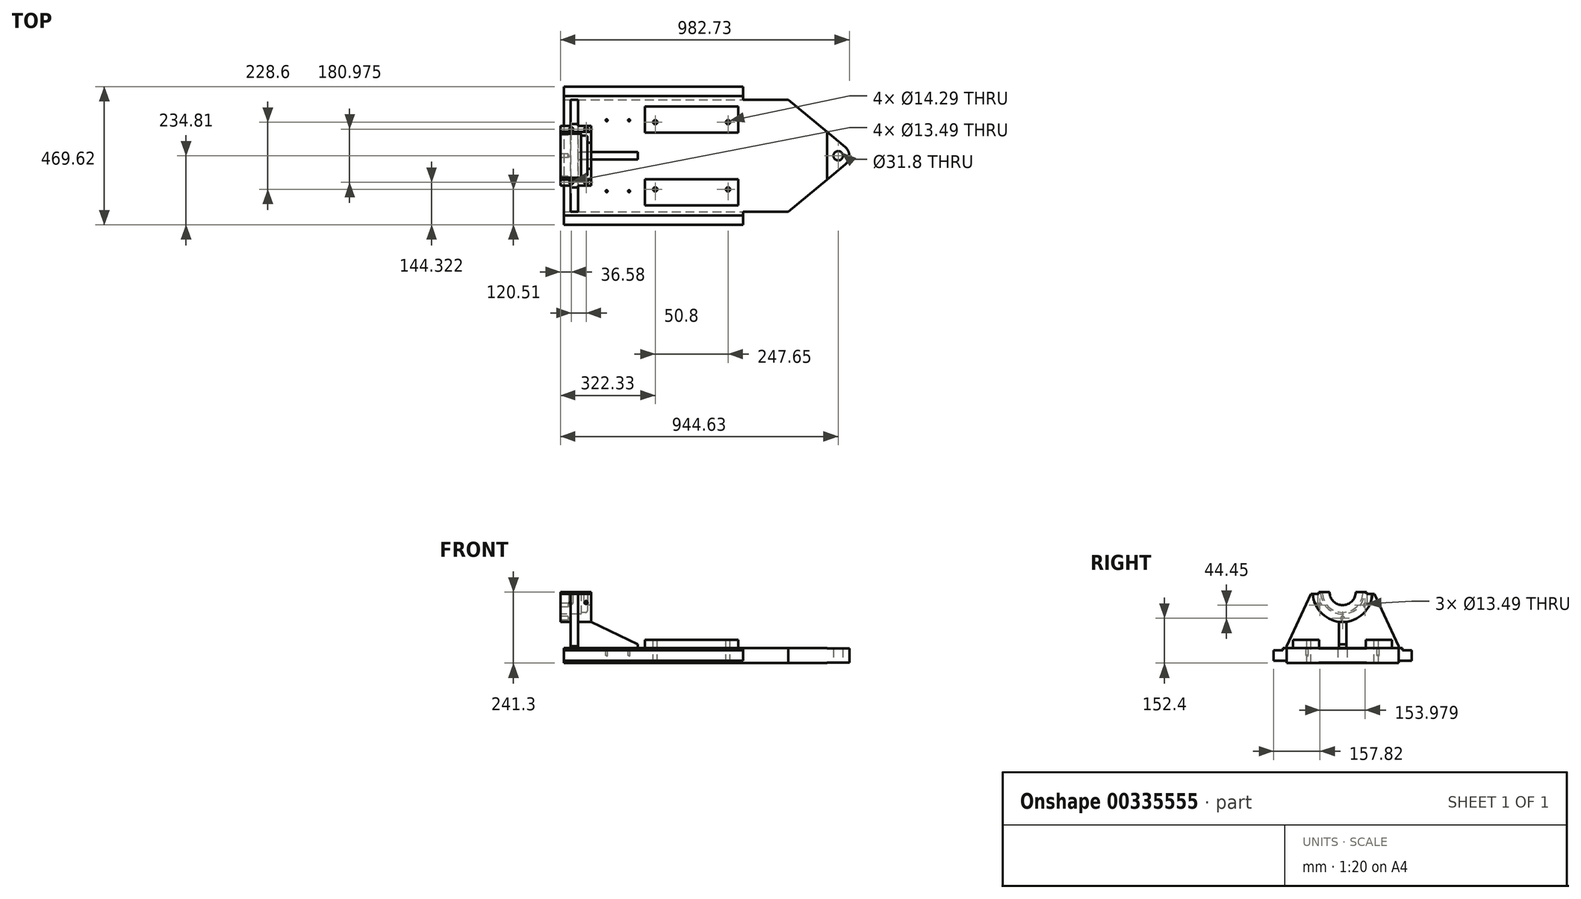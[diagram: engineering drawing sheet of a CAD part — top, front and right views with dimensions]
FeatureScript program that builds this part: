
annotation { "Feature Type Name" : "Feature", "Feature Type Description" : "" }
export const myFeature = defineFeature(function(context is Context, id is Id, definition is map)
    precondition{}
    {
        {
            var Q0;
            Q0=qCreatedBy(makeId("Top.planeOp"),FACE);
            var sketch = newSketch(context, id + "F0", { "sketchPlane" : qUnion([Q0])});
            skLineSegment(sketch, "E0.bottom", {"start": v(-304.8, 234.81) * mm, "end": v(304.8, 234.81) * mm});
            skLineSegment(sketch, "E0.top", {"start": v(-304.8, -234.81) * mm, "end": v(304.8, -234.81) * mm});
            skLineSegment(sketch, "E0.left", {"start": v(-304.8, 234.81) * mm, "end": v(-304.8, -234.81) * mm});
            skPoint(sketch, "E0.middle", {"position": v(0, 0) * mm});
            skLineSegment(sketch, "E1.0", {"start": v(666.75, 234.81) * mm, "end": v(666.75, -234.81) * mm, "construction": true});
            skLineSegment(sketch, "E2.0", {"start": v(628.65, 234.81) * mm, "end": v(628.65, -234.81) * mm, "construction": true});
            skLineSegment(sketch, "E3", {"start": v(459.57, 190.5) * mm, "end": v(653.04, 29.27) * mm});
            skLineSegment(sketch, "E4", {"start": v(459.57, -190.5) * mm, "end": v(656.3, -26.56) * mm});
            skLineSegment(sketch, "E5", {"start": v(304.8, 234.81) * mm, "end": v(304.8, 190.5) * mm});
            skLineSegment(sketch, "E6", {"start": v(-414.48, 0) * mm, "end": v(838.18, 0) * mm, "construction": true});
            skArc(sketch, "E7", {"start": v(653.04, -29.27) * mm, "mid": v(666.75, 0) * mm, "end": v(653.04, 29.27) * mm});
            skCircle(sketch, "E8", {"center": v(628.65, 0) * mm, "radius": 15.9 * mm});
            skLineSegment(sketch, "E9.0", {"start": v(-414.48, -190.5) * mm, "end": v(-304.8, -190.5) * mm});
            skLineSegment(sketch, "E10.trimOffspring", {"start": v(304.8, -190.5) * mm, "end": v(459.57, -190.5) * mm});
            skPoint(sketch, "E11.top.end.orphan", {"position": v(406.4, -234.81) * mm});
            skLineSegment(sketch, "E12.trimOffspring", {"start": v(628.65, -190.5) * mm, "end": v(838.18, -190.5) * mm});
            skLineSegment(sketch, "E13.MirrorCS", {"start": v(304.8, 190.5) * mm, "end": v(459.57, 190.5) * mm});
            skLineSegment(sketch, "E14.trimOffspring", {"start": v(304.8, -190.5) * mm, "end": v(304.8, -234.81) * mm});
            skSolve(sketch);
        }
        {
            var Q0;
            Q0=qSketchRegion(id+"F0",true);
            extrude(context, id + "F1", {"entities" : qUnion([Q0]), "endBound" : BoundingType.SYMMETRIC, "depth" : 50.8 * mm});
        }
        {
            var Q0;
            Q0=makeQuery(id+"F1.opExtrude","CAP_FACE",FACE,{"disambiguationData":[OSD([sQuery(id+"F0.wireOp",EDGE,"E0.bottom"),sQuery(id+"F0.wireOp",EDGE,"E0.top"),sQuery(id+"F0.wireOp",EDGE,"E0.left"),sQuery(id+"F0.wireOp",EDGE,"E3"),sQuery(id+"F0.wireOp",EDGE,"E4"),sQuery(id+"F0.wireOp",EDGE,"E5"),sQuery(id+"F0.wireOp",EDGE,"E7"),sQuery(id+"F0.wireOp",EDGE,"E8"),sQuery(id+"F0.wireOp",EDGE,"E10.trimOffspring"),sQuery(id+"F0.wireOp",EDGE,"E13.MirrorCS"),sQuery(id+"F0.wireOp",EDGE,"E14.trimOffspring")])],"isStart":false});
            var sketch = newSketch(context, id + "F2", { "sketchPlane" : qUnion([Q0])});
            skCircle(sketch, "E15.0", {"center": v(628.65, 0) * mm, "radius": 15.9 * mm, "construction": true});
            skLineSegment(sketch, "E16.bottom", {"start": v(590.55, 101.6) * mm, "end": v(666.75, 101.6) * mm});
            skLineSegment(sketch, "E16.top", {"start": v(590.55, -101.6) * mm, "end": v(666.75, -101.6) * mm});
            skLineSegment(sketch, "E16.left", {"start": v(590.55, 101.6) * mm, "end": v(590.55, -101.6) * mm});
            skLineSegment(sketch, "E16.right", {"start": v(666.75, 101.6) * mm, "end": v(666.75, -101.6) * mm});
            skSolve(sketch);
        }
        {
            var Q0;
            Q0=qSketchRegion(id+"F2",true);
            extrude(context, id + "F3", {"entities" : qUnion([Q0]), "operationType" : NewBodyOperationType.REMOVE, "oppositeDirection" : true, "depth" : 1.59 * mm});
        }
        {
            var Q0;
            Q0=makeQuery(id+"F1.opExtrude","CAP_FACE",FACE,{"disambiguationData":[OSD([sQuery(id+"F0.wireOp",EDGE,"E0.bottom"),sQuery(id+"F0.wireOp",EDGE,"E0.top"),sQuery(id+"F0.wireOp",EDGE,"E0.left"),sQuery(id+"F0.wireOp",EDGE,"E3"),sQuery(id+"F0.wireOp",EDGE,"E4"),sQuery(id+"F0.wireOp",EDGE,"E5"),sQuery(id+"F0.wireOp",EDGE,"E7"),sQuery(id+"F0.wireOp",EDGE,"E8"),sQuery(id+"F0.wireOp",EDGE,"E10.trimOffspring"),sQuery(id+"F0.wireOp",EDGE,"E13.MirrorCS"),sQuery(id+"F0.wireOp",EDGE,"E14.trimOffspring")])],"isStart":true});
            var sketch = newSketch(context, id + "F4", { "sketchPlane" : qUnion([Q0])});
            skCircle(sketch, "E17.0", {"center": v(628.65, 0) * mm, "radius": 15.9 * mm, "construction": true});
            skLineSegment(sketch, "E18.bottom", {"start": v(590.55, 101.6) * mm, "end": v(666.75, 101.6) * mm});
            skLineSegment(sketch, "E18.top", {"start": v(590.55, -101.6) * mm, "end": v(666.75, -101.6) * mm});
            skLineSegment(sketch, "E18.left", {"start": v(590.55, 101.6) * mm, "end": v(590.55, -101.6) * mm});
            skLineSegment(sketch, "E18.right", {"start": v(666.75, 101.6) * mm, "end": v(666.75, -101.6) * mm});
            skSolve(sketch);
        }
        {
            var Q0;
            Q0=qSketchRegion(id+"F4",true);
            extrude(context, id + "F5", {"entities" : qUnion([Q0]), "operationType" : NewBodyOperationType.REMOVE, "oppositeDirection" : true, "depth" : 1.59 * mm});
        }
        {
            var Q0;
            Q0=makeQuery(id+"F1.opExtrude","CAP_FACE",FACE,{"disambiguationData":[OSD([sQuery(id+"F0.wireOp",EDGE,"E0.bottom"),sQuery(id+"F0.wireOp",EDGE,"E0.top"),sQuery(id+"F0.wireOp",EDGE,"E0.left"),sQuery(id+"F0.wireOp",EDGE,"E3"),sQuery(id+"F0.wireOp",EDGE,"E4"),sQuery(id+"F0.wireOp",EDGE,"E5"),sQuery(id+"F0.wireOp",EDGE,"E7"),sQuery(id+"F0.wireOp",EDGE,"E8"),sQuery(id+"F0.wireOp",EDGE,"E10.trimOffspring"),sQuery(id+"F0.wireOp",EDGE,"E13.MirrorCS"),sQuery(id+"F0.wireOp",EDGE,"E14.trimOffspring")])],"isStart":false});
            var sketch = newSketch(context, id + "F6", { "sketchPlane" : qUnion([Q0])});
            skLineSegment(sketch, "E19", {"start": v(-362.8, 0) * mm, "end": v(684.09, 0) * mm, "construction": true});
            skLineSegment(sketch, "E20.0", {"start": v(-362.8, -203.2) * mm, "end": v(684.09, -203.2) * mm, "construction": true});
            skLineSegment(sketch, "E21.0", {"start": v(-304.8, 234.81) * mm, "end": v(-304.8, -234.81) * mm, "construction": true});
            skLineSegment(sketch, "E22.0", {"start": v(304.8, -190.5) * mm, "end": v(304.8, -234.81) * mm, "construction": true});
            skLineSegment(sketch, "E23.bottom", {"start": v(-304.8, -234.81) * mm, "end": v(332.24, -234.81) * mm});
            skLineSegment(sketch, "E23.top", {"start": v(-304.8, -203.2) * mm, "end": v(332.24, -203.2) * mm});
            skLineSegment(sketch, "E23.left", {"start": v(-304.8, -234.81) * mm, "end": v(-304.8, -203.2) * mm});
            skLineSegment(sketch, "E23.right", {"start": v(332.24, -234.81) * mm, "end": v(332.24, -203.2) * mm});
            skLineSegment(sketch, "E24.MirrorCS", {"start": v(332.24, 234.81) * mm, "end": v(332.24, 203.2) * mm});
            skLineSegment(sketch, "E25.MirrorCS", {"start": v(-304.8, 234.81) * mm, "end": v(-304.8, 203.2) * mm});
            skLineSegment(sketch, "E26.MirrorCS", {"start": v(-304.8, 203.2) * mm, "end": v(332.24, 203.2) * mm});
            skLineSegment(sketch, "E27.MirrorCS", {"start": v(-304.8, 234.81) * mm, "end": v(332.24, 234.81) * mm});
            skLineSegment(sketch, "E28.MirrorCS", {"start": v(304.8, 190.5) * mm, "end": v(304.8, 234.81) * mm, "construction": true});
            skSolve(sketch);
        }
        {
            var Q0;
            Q0=qSketchRegion(id+"F6",true);
            extrude(context, id + "F7", {"entities" : qUnion([Q0]), "operationType" : NewBodyOperationType.REMOVE, "oppositeDirection" : true, "depth" : 7.94 * mm});
        }
        {
            var Q0;
            Q0=makeQuery(id+"F1.opExtrude","CAP_FACE",FACE,{"disambiguationData":[OSD([sQuery(id+"F0.wireOp",EDGE,"E0.bottom"),sQuery(id+"F0.wireOp",EDGE,"E0.top"),sQuery(id+"F0.wireOp",EDGE,"E0.left"),sQuery(id+"F0.wireOp",EDGE,"E3"),sQuery(id+"F0.wireOp",EDGE,"E4"),sQuery(id+"F0.wireOp",EDGE,"E5"),sQuery(id+"F0.wireOp",EDGE,"E7"),sQuery(id+"F0.wireOp",EDGE,"E8"),sQuery(id+"F0.wireOp",EDGE,"E10.trimOffspring"),sQuery(id+"F0.wireOp",EDGE,"E13.MirrorCS"),sQuery(id+"F0.wireOp",EDGE,"E14.trimOffspring")])],"isStart":true});
            var sketch = newSketch(context, id + "F8", { "sketchPlane" : qUnion([Q0])});
            skLineSegment(sketch, "E29", {"start": v(-400.34, 0) * mm, "end": v(753.76, 0) * mm, "construction": true});
            skLineSegment(sketch, "E30.0", {"start": v(-304.8, -234.81) * mm, "end": v(-304.8, 234.81) * mm, "construction": true});
            skLineSegment(sketch, "E31.0", {"start": v(-400.34, -190.5) * mm, "end": v(753.76, -190.5) * mm, "construction": true});
            skLineSegment(sketch, "E32.bottom", {"start": v(-304.8, -190.5) * mm, "end": v(475.01, -190.5) * mm});
            skLineSegment(sketch, "E32.top", {"start": v(-304.8, -283.73) * mm, "end": v(475.01, -283.73) * mm});
            skLineSegment(sketch, "E32.left", {"start": v(-304.8, -190.5) * mm, "end": v(-304.8, -283.73) * mm});
            skLineSegment(sketch, "E32.right", {"start": v(475.01, -190.5) * mm, "end": v(475.01, -283.73) * mm});
            skLineSegment(sketch, "E33.MirrorCS", {"start": v(475.01, 190.5) * mm, "end": v(475.01, 283.73) * mm});
            skLineSegment(sketch, "E34.MirrorCS", {"start": v(-304.8, 190.5) * mm, "end": v(-304.8, 283.73) * mm});
            skLineSegment(sketch, "E35.MirrorCS", {"start": v(-304.8, 283.73) * mm, "end": v(475.01, 283.73) * mm});
            skLineSegment(sketch, "E36.MirrorCS", {"start": v(-304.8, 190.5) * mm, "end": v(475.01, 190.5) * mm});
            skSolve(sketch);
        }
        {
            var Q0;
            Q0=qSketchRegion(id+"F8",true);
            extrude(context, id + "F9", {"entities" : qUnion([Q0]), "operationType" : NewBodyOperationType.REMOVE, "oppositeDirection" : true, "depth" : 7.94 * mm});
        }
        {
            var Q0;
            Q0=makeQuery(id+"F1.opExtrude","CAP_FACE",FACE,{"disambiguationData":[OSD([sQuery(id+"F0.wireOp",EDGE,"E0.bottom"),sQuery(id+"F0.wireOp",EDGE,"E0.top"),sQuery(id+"F0.wireOp",EDGE,"E0.left"),sQuery(id+"F0.wireOp",EDGE,"E3"),sQuery(id+"F0.wireOp",EDGE,"E4"),sQuery(id+"F0.wireOp",EDGE,"E5"),sQuery(id+"F0.wireOp",EDGE,"E7"),sQuery(id+"F0.wireOp",EDGE,"E8"),sQuery(id+"F0.wireOp",EDGE,"E10.trimOffspring"),sQuery(id+"F0.wireOp",EDGE,"E13.MirrorCS"),sQuery(id+"F0.wireOp",EDGE,"E14.trimOffspring")])],"isStart":false});
            var sketch = newSketch(context, id + "F10", { "sketchPlane" : qUnion([Q0])});
            skLineSegment(sketch, "E37", {"start": v(-417.52, 0) * mm, "end": v(724.3, 0) * mm, "construction": true});
            skLineSegment(sketch, "E38.0", {"start": v(-304.8, 203.2) * mm, "end": v(-304.8, -203.2) * mm, "construction": true});
            skLineSegment(sketch, "E39.0", {"start": v(-28.57, 203.2) * mm, "end": v(-28.57, -203.2) * mm, "construction": true});
            skLineSegment(sketch, "E40.0", {"start": v(288.93, 203.2) * mm, "end": v(288.93, -203.2) * mm, "construction": true});
            skLineSegment(sketch, "E41.0", {"start": v(-417.52, -79.38) * mm, "end": v(724.3, -79.38) * mm, "construction": true});
            skLineSegment(sketch, "E42.bottom", {"start": v(-28.57, -79.38) * mm, "end": v(288.93, -79.38) * mm});
            skLineSegment(sketch, "E42.top", {"start": v(-28.57, -168.28) * mm, "end": v(288.93, -168.28) * mm});
            skLineSegment(sketch, "E42.left", {"start": v(-28.57, -79.38) * mm, "end": v(-28.57, -168.28) * mm});
            skLineSegment(sketch, "E42.right", {"start": v(288.93, -79.38) * mm, "end": v(288.93, -168.28) * mm});
            skLineSegment(sketch, "E43.MirrorCS", {"start": v(-28.57, 168.28) * mm, "end": v(288.93, 168.28) * mm});
            skLineSegment(sketch, "E44.MirrorCS", {"start": v(288.93, 79.38) * mm, "end": v(288.93, 168.28) * mm});
            skLineSegment(sketch, "E45.MirrorCS", {"start": v(-28.57, 79.38) * mm, "end": v(-28.57, 168.28) * mm});
            skLineSegment(sketch, "E46.MirrorCS", {"start": v(-28.57, 79.38) * mm, "end": v(288.93, 79.38) * mm});
            skSolve(sketch);
        }
        {
            var Q0;
            Q0=qSketchRegion(id+"F10",true);
            extrude(context, id + "F11", {"entities" : qUnion([Q0]), "operationType" : NewBodyOperationType.ADD, "depth" : 28.57 * mm});
        }
        {
            var Q0;
            Q0=makeQuery(id+"F11.opExtrude","CAP_FACE",FACE,{"disambiguationData":[OSD([sQuery(id+"F10.wireOp",EDGE,"E43.MirrorCS"),sQuery(id+"F10.wireOp",EDGE,"E44.MirrorCS"),sQuery(id+"F10.wireOp",EDGE,"E45.MirrorCS"),sQuery(id+"F10.wireOp",EDGE,"E46.MirrorCS")])],"isStart":false});
            var sketch = newSketch(context, id + "F12", { "sketchPlane" : qUnion([Q0])});
            skCircle(sketch, "E47.0", {"center": v(628.65, 0) * mm, "radius": 15.9 * mm, "construction": true});
            skLineSegment(sketch, "E48", {"start": v(628.65, 0) * mm, "end": v(628.65, 304) * mm, "construction": true});
            skLineSegment(sketch, "E49", {"start": v(-454.06, 0) * mm, "end": v(702.68, 0) * mm, "construction": true});
            skLineSegment(sketch, "E50.0", {"start": v(-454.06, 114.3) * mm, "end": v(702.68, 114.3) * mm, "construction": true});
            skLineSegment(sketch, "E51.0", {"start": v(254, 0) * mm, "end": v(254, 304) * mm, "construction": true});
            skLineSegment(sketch, "E52.0", {"start": v(6.35, 0) * mm, "end": v(6.35, 304) * mm, "construction": true});
            skPoint(sketch, "E53", {"position": v(6.35, 114.3) * mm});
            skPoint(sketch, "E54", {"position": v(254, 114.3) * mm});
            skPoint(sketch, "E55.MirrorP", {"position": v(254, -114.3) * mm});
            skPoint(sketch, "E56.MirrorP", {"position": v(6.35, -114.3) * mm});
            skSolve(sketch);
        }
        {
            var Q0;
            Q0=sQuery(id+"F12.wireOp",VERTEX,"E53");
            var Q1;
            Q1=sQuery(id+"F12.wireOp",VERTEX,"E54");
            var Q2;
            Q2=sQuery(id+"F12.wireOp",VERTEX,"E56.MirrorP");
            var Q3;
            Q3=sQuery(id+"F12.wireOp",VERTEX,"E55.MirrorP");
            var Q4;
            Q4=makeQuery(id+"F1.opExtrude","SWEPT_BODY",BODY,{"disambiguationData":[OSD([sQuery(id+"F0.wireOp",EDGE,"E0.bottom"),sQuery(id+"F0.wireOp",EDGE,"E0.top"),sQuery(id+"F0.wireOp",EDGE,"E0.left"),sQuery(id+"F0.wireOp",EDGE,"E3"),sQuery(id+"F0.wireOp",EDGE,"E4"),sQuery(id+"F0.wireOp",EDGE,"E5"),sQuery(id+"F0.wireOp",EDGE,"E7"),sQuery(id+"F0.wireOp",EDGE,"E8"),sQuery(id+"F0.wireOp",EDGE,"E10.trimOffspring"),sQuery(id+"F0.wireOp",EDGE,"E13.MirrorCS"),sQuery(id+"F0.wireOp",EDGE,"E14.trimOffspring")])]});
            hole(context, id + "F13", {"style" : HoleStyle.SIMPLE, "endStyle" : HoleEndStyle.THROUGH, "holeDiameter" : 14.29 * mm, "tappedDepth" : 19.53 * mm, "tapClearance" : 3, "locations" : qUnion([Q0, Q1, Q2, Q3]), "scope" : qUnion([Q4])});
        }
        {
            var Q0;
            Q0=makeQuery(id+"F1.opExtrude","CAP_FACE",FACE,{"disambiguationData":[OSD([sQuery(id+"F0.wireOp",EDGE,"E0.bottom"),sQuery(id+"F0.wireOp",EDGE,"E0.top"),sQuery(id+"F0.wireOp",EDGE,"E0.left"),sQuery(id+"F0.wireOp",EDGE,"E3"),sQuery(id+"F0.wireOp",EDGE,"E4"),sQuery(id+"F0.wireOp",EDGE,"E5"),sQuery(id+"F0.wireOp",EDGE,"E7"),sQuery(id+"F0.wireOp",EDGE,"E8"),sQuery(id+"F0.wireOp",EDGE,"E10.trimOffspring"),sQuery(id+"F0.wireOp",EDGE,"E13.MirrorCS"),sQuery(id+"F0.wireOp",EDGE,"E14.trimOffspring")])],"isStart":false});
            var sketch = newSketch(context, id + "F14", { "sketchPlane" : qUnion([Q0])});
            skLineSegment(sketch, "E57.0", {"start": v(-304.8, 203.2) * mm, "end": v(-304.8, -203.2) * mm, "construction": true});
            skLineSegment(sketch, "E58.0", {"start": v(-280.99, 203.2) * mm, "end": v(-280.99, -203.2) * mm, "construction": true});
            skLineSegment(sketch, "E59", {"start": v(-408.3, 0) * mm, "end": v(198.31, 0) * mm, "construction": true});
            skLineSegment(sketch, "E60.0", {"start": v(-408.3, -190.5) * mm, "end": v(198.31, -190.5) * mm, "construction": true});
            skLineSegment(sketch, "E61.bottom", {"start": v(-280.99, -190.5) * mm, "end": v(-255.59, -190.5) * mm});
            skLineSegment(sketch, "E61.top", {"start": v(-280.99, 190.5) * mm, "end": v(-255.59, 190.5) * mm});
            skLineSegment(sketch, "E61.left", {"start": v(-280.99, -190.5) * mm, "end": v(-280.99, 190.5) * mm});
            skLineSegment(sketch, "E61.right", {"start": v(-255.59, -190.5) * mm, "end": v(-255.59, 190.5) * mm});
            skSolve(sketch);
        }
        {
            var Q0;
            Q0=qSketchRegion(id+"F14",true);
            extrude(context, id + "F15", {"entities" : qUnion([Q0]), "operationType" : NewBodyOperationType.ADD, "depth" : 190.5 * mm});
        }
        {
            var Q0;
            Q0=makeQuery(id+"F1.opExtrude","SWEPT_FACE",FACE,{"disambiguationData":[OSD([sQuery(id+"F0.wireOp",EDGE,"E0.left")])]});
            cPlane(context, id + "F16", {"entities" : qUnion([Q0]), "cplaneType" : CPlaneType.OFFSET, "offset" : 11.18 * mm, "width" : 152.4 * mm, "height" : 152.4 * mm});
        }
        {
            var Q0;
            Q0=qCreatedBy(id+"F16.planeOp",FACE);
            var sketch = newSketch(context, id + "F17", { "sketchPlane" : qUnion([Q0])});
            skLineSegment(sketch, "E62.0", {"start": v(190.5, 215.9) * mm, "end": v(-190.5, 215.9) * mm, "construction": true});
            skLineSegment(sketch, "E63", {"start": v(0, 334.76) * mm, "end": v(0, -159.92) * mm, "construction": true});
            skCircle(sketch, "E64", {"center": v(0, 215.9) * mm, "radius": 101.6 * mm});
            skSolve(sketch);
        }
        {
            var Q0;
            Q0=qSketchRegion(id+"F17",true);
            extrude(context, id + "F18", {"entities" : qUnion([Q0]), "operationType" : NewBodyOperationType.ADD, "oppositeDirection" : true, "depth" : 104.77 * mm});
        }
        {
            var Q0;
            Q0=makeQuery(id+"F15.opExtrude","SWEPT_FACE",FACE,{"disambiguationData":[OSD([sQuery(id+"F14.wireOp",EDGE,"E61.left")])]});
            var sketch = newSketch(context, id + "F19", { "sketchPlane" : qUnion([Q0])});
            skCircle(sketch, "E65.0", {"center": v(0, 215.9) * mm, "radius": 101.6 * mm, "construction": true});
            skLineSegment(sketch, "E66.0", {"start": v(-203.2, 31.75) * mm, "end": v(203.2, 31.75) * mm, "construction": true});
            skLineSegment(sketch, "E67.0", {"start": v(-190.5, 215.9) * mm, "end": v(-190.5, 25.4) * mm, "construction": true});
            skLineSegment(sketch, "E68", {"start": v(-190.5, 31.75) * mm, "end": v(-107.95, 209.55) * mm});
            skLineSegment(sketch, "E69", {"start": v(-107.95, 209.55) * mm, "end": v(-80.96, 209.55) * mm});
            skLineSegment(sketch, "E70", {"start": v(-80.96, 209.55) * mm, "end": v(-80.96, 215.9) * mm});
            skLineSegment(sketch, "E71", {"start": v(-80.96, 215.9) * mm, "end": v(0, 215.9) * mm});
            skLineSegment(sketch, "E72", {"start": v(0, 356.38) * mm, "end": v(0, -105.82) * mm, "construction": true});
            skLineSegment(sketch, "E73.MirrorCS", {"start": v(80.96, 209.55) * mm, "end": v(80.96, 215.9) * mm});
            skLineSegment(sketch, "E74.MirrorCS", {"start": v(80.96, 215.9) * mm, "end": v(0, 215.9) * mm});
            skLineSegment(sketch, "E75.MirrorCS", {"start": v(190.5, 31.75) * mm, "end": v(107.95, 209.55) * mm});
            skLineSegment(sketch, "E76.MirrorCS", {"start": v(190.5, 215.9) * mm, "end": v(190.5, 25.4) * mm, "construction": true});
            skLineSegment(sketch, "E77.MirrorCS", {"start": v(107.95, 209.55) * mm, "end": v(80.96, 209.55) * mm});
            skLineSegment(sketch, "E78", {"start": v(-190.5, 31.75) * mm, "end": v(-190.5, 348.54) * mm});
            skLineSegment(sketch, "E79", {"start": v(-190.5, 348.54) * mm, "end": v(190.5, 348.54) * mm});
            skLineSegment(sketch, "E80", {"start": v(190.5, 348.54) * mm, "end": v(190.5, 31.75) * mm});
            skSolve(sketch);
        }
        {
            var Q0;
            Q0=qSketchRegion(id+"F19",true);
            extrude(context, id + "F20", {"entities" : qUnion([Q0]), "operationType" : NewBodyOperationType.REMOVE, "endBound" : BoundingType.SYMMETRIC, "oppositeDirection" : true, "depth" : 152.4 * mm});
        }
        {
            var Q0;
            Q0=makeQuery(id+"F18.opExtrude","CAP_FACE",FACE,{"disambiguationData":[OSD([sQuery(id+"F17.wireOp",EDGE,"E64")])],"isStart":true});
            var sketch = newSketch(context, id + "F21", { "sketchPlane" : qUnion([Q0])});
            skCircle(sketch, "E81", {"center": v(0, 215.9) * mm, "radius": 44.45 * mm});
            skSolve(sketch);
        }
        {
            var Q0;
            Q0=qSketchRegion(id+"F21",true);
            extrude(context, id + "F22", {"entities" : qUnion([Q0]), "operationType" : NewBodyOperationType.REMOVE, "endBound" : BoundingType.THROUGH_ALL, "oppositeDirection" : true, "depth" : 25.4 * mm});
        }
        {
            var Q0;
            Q0=makeQuery(id+"F18.opExtrude","CAP_FACE",FACE,{"disambiguationData":[OSD([sQuery(id+"F17.wireOp",EDGE,"E64")])],"isStart":true});
            var sketch = newSketch(context, id + "F23", { "sketchPlane" : qUnion([Q0])});
            skArc(sketch, "E82.0", {"start": v(-44.45, 215.9) * mm, "mid": v(0, 171.45) * mm, "end": v(44.45, 215.9) * mm, "construction": true});
            skCircle(sketch, "E83", {"center": v(0, 215.9) * mm, "radius": 69.09 * mm});
            skSolve(sketch);
        }
        {
            var Q0;
            Q0=qSketchRegion(id+"F23",true);
            extrude(context, id + "F24", {"entities" : qUnion([Q0]), "operationType" : NewBodyOperationType.REMOVE, "oppositeDirection" : true, "depth" : 92.07 * mm});
        }
        {
            var Q0;
            Q0=makeQuery(id+"F18.opExtrude","CAP_FACE",FACE,{"disambiguationData":[OSD([sQuery(id+"F17.wireOp",EDGE,"E64")])],"isStart":true});
            var sketch = newSketch(context, id + "F25", { "sketchPlane" : qUnion([Q0])});
            skArc(sketch, "E84.0", {"start": v(44.45, 215.9) * mm, "mid": v(0, 171.45) * mm, "end": v(-44.45, 215.9) * mm, "construction": true});
            skCircle(sketch, "E85", {"center": v(0, 215.9) * mm, "radius": 74.93 * mm});
            skSolve(sketch);
        }
        {
            var Q0;
            Q0=qSketchRegion(id+"F25",true);
            extrude(context, id + "F26", {"entities" : qUnion([Q0]), "operationType" : NewBodyOperationType.REMOVE, "oppositeDirection" : true, "depth" : 69.85 * mm});
        }
        {
            var Q0;
            Q0=makeQuery(id+"F20.boolean.opBoolean","COPY",FACE,{"derivedFrom":makeQuery(id+"F20.opExtrude","SWEPT_FACE",FACE,{"disambiguationData":[OSD([sQuery(id+"F19.wireOp",EDGE,"E69")])]})});
            var sketch = newSketch(context, id + "F27", { "sketchPlane" : qUnion([Q0])});
            skLineSegment(sketch, "E86", {"start": v(-429.52, 0) * mm, "end": v(-135.24, 0) * mm, "construction": true});
            skLineSegment(sketch, "E87.0", {"start": v(-315.98, 101.4) * mm, "end": v(-315.98, 80.96) * mm, "construction": true});
            skLineSegment(sketch, "E88.0", {"start": v(-429.52, 90.49) * mm, "end": v(-135.24, 90.49) * mm, "construction": true});
            skLineSegment(sketch, "E89.0", {"start": v(-279.4, 101.4) * mm, "end": v(-279.4, 80.96) * mm, "construction": true});
            skLineSegment(sketch, "E90.0", {"start": v(-228.6, 101.4) * mm, "end": v(-228.6, 80.96) * mm, "construction": true});
            skPoint(sketch, "E91", {"position": v(-279.4, 90.49) * mm});
            skPoint(sketch, "E92", {"position": v(-228.6, 90.49) * mm});
            skPoint(sketch, "E93.MirrorP", {"position": v(-279.4, -90.49) * mm});
            skPoint(sketch, "E94.MirrorP", {"position": v(-228.6, -90.49) * mm});
            skSolve(sketch);
        }
        {
            var Q0;
            Q0=sQuery(id+"F27.wireOp",VERTEX,"E91");
            var Q1;
            Q1=sQuery(id+"F27.wireOp",VERTEX,"E92");
            var Q2;
            Q2=sQuery(id+"F27.wireOp",VERTEX,"E93.MirrorP");
            var Q3;
            Q3=sQuery(id+"F27.wireOp",VERTEX,"E94.MirrorP");
            var Q4;
            Q4=makeQuery(id+"F1.opExtrude","SWEPT_BODY",BODY,{"disambiguationData":[OSD([sQuery(id+"F0.wireOp",EDGE,"E0.bottom"),sQuery(id+"F0.wireOp",EDGE,"E0.top"),sQuery(id+"F0.wireOp",EDGE,"E0.left"),sQuery(id+"F0.wireOp",EDGE,"E3"),sQuery(id+"F0.wireOp",EDGE,"E4"),sQuery(id+"F0.wireOp",EDGE,"E5"),sQuery(id+"F0.wireOp",EDGE,"E7"),sQuery(id+"F0.wireOp",EDGE,"E8"),sQuery(id+"F0.wireOp",EDGE,"E10.trimOffspring"),sQuery(id+"F0.wireOp",EDGE,"E13.MirrorCS"),sQuery(id+"F0.wireOp",EDGE,"E14.trimOffspring")])]});
            hole(context, id + "F28", {"style" : HoleStyle.SIMPLE, "endStyle" : HoleEndStyle.BLIND, "standardTappedOrClearance" : lookupTablePath({ "standard" : "ANSI", "fit" : "Normal (ASME)", "size" : "1/2", "type" : "Clearance" }), "standardBlindInLast" : lookupTablePath({ "fit" : "Free", "standard" : "ANSI", "size" : "1/2", "type" : "Clearance" }), "holeDiameter" : 13.5 * mm, "holeDepth" : 31.75 * mm, "tappedDepth" : 19.53 * mm, "tapClearance" : 3, "locations" : qUnion([Q0, Q1, Q2, Q3]), "scope" : qUnion([Q4])});
        }
        {
            var Q0;
            Q0=qCreatedBy(makeId("Front.planeOp"),FACE);
            var sketch = newSketch(context, id + "F29", { "sketchPlane" : qUnion([Q0])});
            skLineSegment(sketch, "E95", {"start": v(-211.2, 114.3) * mm, "end": v(-255.59, 114.3) * mm});
            skLineSegment(sketch, "E96.0", {"start": v(-304.8, 25.4) * mm, "end": v(304.8, 25.4) * mm});
            skLineSegment(sketch, "E97.0", {"start": v(-255.59, 31.75) * mm, "end": v(-255.59, 209.55) * mm});
            skLineSegment(sketch, "E98.0", {"start": v(-255.59, 31.75) * mm, "end": v(-255.59, 25.4) * mm});
            skLineSegment(sketch, "E99.0", {"start": v(-52.39, 25.4) * mm, "end": v(-52.39, 209.55) * mm});
            skLineSegment(sketch, "E100.0", {"start": v(-304.8, 38.1) * mm, "end": v(304.8, 38.1) * mm, "construction": true});
            skLineSegment(sketch, "E101", {"start": v(-211.2, 114.3) * mm, "end": v(-52.39, 38.1) * mm});
            skSolve(sketch);
        }
        {
            var Q0;
            Q0=qSketchRegion(id+"F29",true);
            extrude(context, id + "F30", {"entities" : qUnion([Q0]), "endBound" : BoundingType.SYMMETRIC, "depth" : 25.4 * mm});
        }
        {
            var Q0;
            Q0=makeQuery(id+"F1.opExtrude","CAP_FACE",FACE,{"disambiguationData":[OSD([sQuery(id+"F0.wireOp",EDGE,"E0.bottom"),sQuery(id+"F0.wireOp",EDGE,"E0.top"),sQuery(id+"F0.wireOp",EDGE,"E0.left"),sQuery(id+"F0.wireOp",EDGE,"E3"),sQuery(id+"F0.wireOp",EDGE,"E4"),sQuery(id+"F0.wireOp",EDGE,"E5"),sQuery(id+"F0.wireOp",EDGE,"E7"),sQuery(id+"F0.wireOp",EDGE,"E8"),sQuery(id+"F0.wireOp",EDGE,"E10.trimOffspring"),sQuery(id+"F0.wireOp",EDGE,"E13.MirrorCS"),sQuery(id+"F0.wireOp",EDGE,"E14.trimOffspring")])],"isStart":false});
            var sketch = newSketch(context, id + "F31", { "sketchPlane" : qUnion([Q0])});
            skCircle(sketch, "E102.0", {"center": v(6.35, 114.3) * mm, "radius": 7.14 * mm, "construction": true});
            skLineSegment(sketch, "E103", {"start": v(6.35, 114.3) * mm, "end": v(6.35, -303.64) * mm, "construction": true});
            skLineSegment(sketch, "E104", {"start": v(-451.94, 0) * mm, "end": v(697.13, 0) * mm, "construction": true});
            skLineSegment(sketch, "E105.0", {"start": v(-82.55, 114.3) * mm, "end": v(-82.55, -303.64) * mm, "construction": true});
            skLineSegment(sketch, "E106.0", {"start": v(-158.75, 114.3) * mm, "end": v(-158.75, -303.64) * mm, "construction": true});
            skLineSegment(sketch, "E107.0", {"start": v(-451.94, -120.65) * mm, "end": v(697.13, -120.65) * mm, "construction": true});
            skPoint(sketch, "E108", {"position": v(-158.75, -120.65) * mm});
            skPoint(sketch, "E109", {"position": v(-82.55, -120.65) * mm});
            skPoint(sketch, "E110.MirrorP", {"position": v(-158.75, 120.65) * mm});
            skPoint(sketch, "E111.MirrorP", {"position": v(-82.55, 120.65) * mm});
            skSolve(sketch);
        }
        {
            var Q0;
            Q0=sQuery(id+"F31.wireOp",VERTEX,"E111.MirrorP");
            var Q1;
            Q1=sQuery(id+"F31.wireOp",VERTEX,"E110.MirrorP");
            var Q2;
            Q2=sQuery(id+"F31.wireOp",VERTEX,"E109");
            var Q3;
            Q3=sQuery(id+"F31.wireOp",VERTEX,"E108");
            var Q4;
            Q4=makeQuery(id+"F1.opExtrude","SWEPT_BODY",BODY,{"disambiguationData":[OSD([sQuery(id+"F0.wireOp",EDGE,"E0.bottom"),sQuery(id+"F0.wireOp",EDGE,"E0.top"),sQuery(id+"F0.wireOp",EDGE,"E0.left"),sQuery(id+"F0.wireOp",EDGE,"E3"),sQuery(id+"F0.wireOp",EDGE,"E4"),sQuery(id+"F0.wireOp",EDGE,"E5"),sQuery(id+"F0.wireOp",EDGE,"E7"),sQuery(id+"F0.wireOp",EDGE,"E8"),sQuery(id+"F0.wireOp",EDGE,"E10.trimOffspring"),sQuery(id+"F0.wireOp",EDGE,"E13.MirrorCS"),sQuery(id+"F0.wireOp",EDGE,"E14.trimOffspring")])]});
            hole(context, id + "F32", {"style" : HoleStyle.SIMPLE, "endStyle" : HoleEndStyle.BLIND, "standardTappedOrClearance" : lookupTablePath({ "standard" : "ANSI", "fit" : "Normal (ASME)", "size" : "1/4", "type" : "Clearance" }), "standardBlindInLast" : lookupTablePath({ "fit" : "Free", "standard" : "ANSI", "size" : "1/4", "type" : "Clearance" }), "holeDiameter" : 6.76 * mm, "holeDepth" : 25.4 * mm, "tappedDepth" : 19.53 * mm, "tapClearance" : 3, "locations" : qUnion([Q0, Q1, Q2, Q3]), "scope" : qUnion([Q4])});
        }
        {
            var Q0;
            Q0=makeQuery(id+"F18.opExtrude","CAP_FACE",FACE,{"disambiguationData":[OSD([sQuery(id+"F17.wireOp",EDGE,"E64")])],"isStart":true});
            var sketch = newSketch(context, id + "F33", { "sketchPlane" : qUnion([Q0])});
            skArc(sketch, "E112.0", {"start": v(44.45, 215.9) * mm, "mid": v(0, 171.45) * mm, "end": v(-44.45, 215.9) * mm, "construction": true});
            skCircle(sketch, "E113", {"center": v(0, 215.9) * mm, "radius": 88.9 * mm, "construction": true});
            skLineSegment(sketch, "E114", {"start": v(0, 215.9) * mm, "end": v(0, -126.02) * mm, "construction": true});
            skLineSegment(sketch, "E115", {"start": v(0, 215.9) * mm, "end": v(325.66, 27.88) * mm, "construction": true});
            skPoint(sketch, "E116", {"position": v(0, 127) * mm});
            skPoint(sketch, "E117", {"position": v(76.99, 171.45) * mm});
            skPoint(sketch, "E118.MirrorP", {"position": v(-76.99, 171.45) * mm});
            skSolve(sketch);
        }
        {
            var Q0;
            Q0=sQuery(id+"F33.wireOp",VERTEX,"E118.MirrorP");
            var Q1;
            Q1=sQuery(id+"F33.wireOp",VERTEX,"E116");
            var Q2;
            Q2=sQuery(id+"F33.wireOp",VERTEX,"E117");
            var Q3;
            Q3=makeQuery(id+"F1.opExtrude","SWEPT_BODY",BODY,{"disambiguationData":[OSD([sQuery(id+"F0.wireOp",EDGE,"E0.bottom"),sQuery(id+"F0.wireOp",EDGE,"E0.top"),sQuery(id+"F0.wireOp",EDGE,"E0.left"),sQuery(id+"F0.wireOp",EDGE,"E3"),sQuery(id+"F0.wireOp",EDGE,"E4"),sQuery(id+"F0.wireOp",EDGE,"E5"),sQuery(id+"F0.wireOp",EDGE,"E7"),sQuery(id+"F0.wireOp",EDGE,"E8"),sQuery(id+"F0.wireOp",EDGE,"E10.trimOffspring"),sQuery(id+"F0.wireOp",EDGE,"E13.MirrorCS"),sQuery(id+"F0.wireOp",EDGE,"E14.trimOffspring")])]});
            hole(context, id + "F34", {"style" : HoleStyle.SIMPLE, "endStyle" : HoleEndStyle.BLIND, "standardTappedOrClearance" : lookupTablePath({ "standard" : "ANSI", "fit" : "Normal (ASME)", "size" : "1/2", "type" : "Clearance" }), "standardBlindInLast" : lookupTablePath({ "fit" : "Free", "standard" : "ANSI", "size" : "1/2", "type" : "Clearance" }), "holeDiameter" : 13.5 * mm, "holeDepth" : 25.4 * mm, "tappedDepth" : 19.53 * mm, "tapClearance" : 3, "locations" : qUnion([Q0, Q1, Q2]), "scope" : qUnion([Q3])});
        }
        {
            var Q0;
            Q0=makeQuery(id+"F24.boolean.opBoolean","COPY",EDGE,{"derivedFrom":makeQuery(id+"F24.opExtrude","CAP_EDGE",EDGE,{"disambiguationData":[OSD([sQuery(id+"F23.wireOp",EDGE,"E83")])],"isStart":false})});
            fillet(context, id + "F35", {"entities" : qUnion([Q0]), "radius" : 6.35 * mm, "tangentPropagation" : true, "allowEdgeOverflow" : false});
        }
        {
            var Q0;
            Q0=makeQuery(id+"F26.boolean.opBoolean","COPY",EDGE,{"derivedFrom":makeQuery(id+"F26.opExtrude","CAP_EDGE",EDGE,{"disambiguationData":[OSD([sQuery(id+"F25.wireOp",EDGE,"E85")])],"isStart":false})});
            fillet(context, id + "F36", {"entities" : qUnion([Q0]), "radius" : 1.59 * mm, "tangentPropagation" : true, "allowEdgeOverflow" : false});
        }
    });
